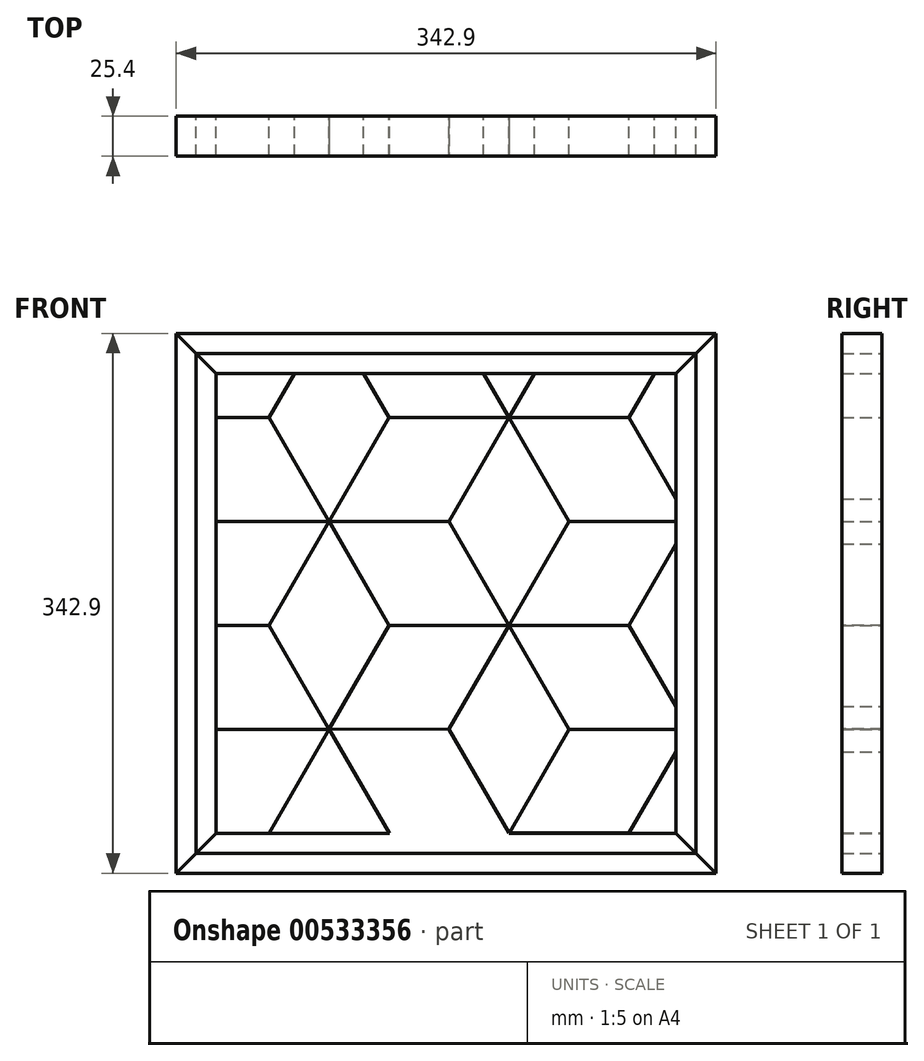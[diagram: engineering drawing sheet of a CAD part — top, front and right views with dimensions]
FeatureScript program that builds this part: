
annotation { "Feature Type Name" : "Feature", "Feature Type Description" : "" }
export const myFeature = defineFeature(function(context is Context, id is Id, definition is map)
    precondition{}
    {
        {
            var Q0;
            Q0=qCreatedBy(makeId("Front.planeOp"),FACE);
            var sketch = newSketch(context, id + "F0", { "sketchPlane" : qUnion([Q0])});
            skLineSegment(sketch, "E0.top", {"start": v(-173.38, -167.67) * mm, "end": v(169.52, -167.67) * mm});
            skLineSegment(sketch, "E0.left", {"start": v(-173.38, 175.23) * mm, "end": v(-173.38, -167.67) * mm});
            skLineSegment(sketch, "E0.right", {"start": v(169.52, 175.23) * mm, "end": v(169.52, -167.67) * mm});
            skLineSegment(sketch, "E1.0", {"start": v(-147.98, 149.83) * mm, "end": v(144.12, 149.83) * mm});
            skLineSegment(sketch, "E1.1", {"start": v(-147.98, 149.83) * mm, "end": v(-147.98, -142.27) * mm});
            skLineSegment(sketch, "E1.2", {"start": v(-147.98, -142.27) * mm, "end": v(144.12, -142.27) * mm});
            skLineSegment(sketch, "E1.3", {"start": v(144.12, 149.83) * mm, "end": v(144.12, -142.27) * mm});
            skLineSegment(sketch, "E2", {"start": v(144.12, 149.83) * mm, "end": v(169.52, 175.23) * mm});
            skLineSegment(sketch, "E3", {"start": v(169.52, -167.67) * mm, "end": v(144.12, -142.27) * mm});
            skLineSegment(sketch, "E4", {"start": v(-173.38, -167.67) * mm, "end": v(-147.98, -142.27) * mm});
            skLineSegment(sketch, "E5", {"start": v(-147.98, 149.83) * mm, "end": v(-173.38, 175.23) * mm});
            skLineSegment(sketch, "E6.0", {"start": v(-76.2, -76.14) * mm, "end": v(-38.1, -10.28) * mm});
            skLineSegment(sketch, "E6.1", {"start": v(-38.1, -10.28) * mm, "end": v(38.1, -10.28) * mm});
            skLineSegment(sketch, "E6.2", {"start": v(38.1, -10.28) * mm, "end": v(76.2, -76.27) * mm});
            skLineSegment(sketch, "E6.3", {"start": v(76.2, -76.27) * mm, "end": v(38.1, -142.27) * mm});
            skLineSegment(sketch, "E6.4", {"start": v(38.1, -142.27) * mm, "end": v(-38.02, -142.27) * mm});
            skLineSegment(sketch, "E6.5", {"start": v(-38.02, -142.27) * mm, "end": v(-76.2, -76.14) * mm});
            skLineSegment(sketch, "E7", {"start": v(-76.2, -76.14) * mm, "end": v(0, -76.27) * mm});
            skLineSegment(sketch, "E8", {"start": v(0, -76.27) * mm, "end": v(38.1, -10.28) * mm});
            skLineSegment(sketch, "E9", {"start": v(0, -76.27) * mm, "end": v(38.1, -142.27) * mm});
            skLineSegment(sketch, "E10.0", {"start": v(-114.3, -10.28) * mm, "end": v(-76.2, 55.7) * mm});
            skLineSegment(sketch, "E10.1", {"start": v(-76.2, 55.7) * mm, "end": v(0, 55.7) * mm});
            skLineSegment(sketch, "E10.2", {"start": v(0, 55.7) * mm, "end": v(38.1, -10.15) * mm});
            skLineSegment(sketch, "E10.3", {"start": v(38.1, -10.15) * mm, "end": v(0, -76.27) * mm});
            skLineSegment(sketch, "E10.4", {"start": v(0, -76.27) * mm, "end": v(-76.2, -76.14) * mm});
            skLineSegment(sketch, "E11", {"start": v(-76.2, 55.7) * mm, "end": v(-38.1, -10.28) * mm});
            skLineSegment(sketch, "E12.0", {"start": v(-38.1, -10.28) * mm, "end": v(-76.2, -76.27) * mm});
            skLineSegment(sketch, "E13", {"start": v(-114.3, -10.28) * mm, "end": v(-147.98, -10.28) * mm});
            skLineSegment(sketch, "E14", {"start": v(38.1, -10.28) * mm, "end": v(114.3, -10.28) * mm});
            skLineSegment(sketch, "E15.0", {"start": v(38.1, -10.15) * mm, "end": v(114.3, -10.15) * mm});
            skLineSegment(sketch, "E15.1", {"start": v(114.3, -10.15) * mm, "end": v(144.12, -61.8) * mm});
            skLineSegment(sketch, "E15.3", {"start": v(114.3, -142.13) * mm, "end": v(38.1, -142.13) * mm});
            skLineSegment(sketch, "E15.4", {"start": v(38.1, -142.13) * mm, "end": v(0, -76.14) * mm});
            skLineSegment(sketch, "E15.5", {"start": v(0, -76.14) * mm, "end": v(38.1, -10.15) * mm});
            skLineSegment(sketch, "E16", {"start": v(144.12, -90.48) * mm, "end": v(114.3, -142.13) * mm});
            skLineSegment(sketch, "E17", {"start": v(76.2, -76.27) * mm, "end": v(144.12, -76.27) * mm});
            skLineSegment(sketch, "E18", {"start": v(144.12, 55.85) * mm, "end": v(76.2, 55.85) * mm});
            skLineSegment(sketch, "E19", {"start": v(114.3, -10.28) * mm, "end": v(144.12, 41.5) * mm});
            skLineSegment(sketch, "E20", {"start": v(-76.2, -76.27) * mm, "end": v(-114.3, -142.27) * mm});
            skLineSegment(sketch, "E21", {"start": v(-76.2, -76.27) * mm, "end": v(-114.3, -10.28) * mm});
            skLineSegment(sketch, "E22", {"start": v(-76.2, -76.27) * mm, "end": v(-147.98, -76.27) * mm});
            skLineSegment(sketch, "E23.0", {"start": v(-38.1, -10.15) * mm, "end": v(-76.2, 55.85) * mm});
            skLineSegment(sketch, "E23.1", {"start": v(-76.2, 55.85) * mm, "end": v(-38.1, 121.84) * mm});
            skLineSegment(sketch, "E23.2", {"start": v(-38.1, 121.84) * mm, "end": v(38.1, 121.84) * mm});
            skLineSegment(sketch, "E23.3", {"start": v(38.1, 121.84) * mm, "end": v(76.2, 55.85) * mm});
            skLineSegment(sketch, "E23.4", {"start": v(76.2, 55.85) * mm, "end": v(38.1, -10.15) * mm});
            skLineSegment(sketch, "E23.5", {"start": v(38.1, -10.15) * mm, "end": v(-38.1, -10.15) * mm});
            skLineSegment(sketch, "E24.0", {"start": v(0, 55.85) * mm, "end": v(-76.2, 55.85) * mm});
            skLineSegment(sketch, "E24.1", {"start": v(-76.2, 55.85) * mm, "end": v(-114.3, 121.84) * mm});
            skLineSegment(sketch, "E24.2", {"start": v(-114.3, 121.84) * mm, "end": v(-98.14, 149.83) * mm});
            skLineSegment(sketch, "E24.4", {"start": v(21.94, 149.83) * mm, "end": v(38.1, 121.84) * mm});
            skLineSegment(sketch, "E24.5", {"start": v(38.1, 121.84) * mm, "end": v(0, 55.85) * mm});
            skLineSegment(sketch, "E25.1", {"start": v(76.2, 55.85) * mm, "end": v(38.1, 121.84) * mm});
            skLineSegment(sketch, "E25.2", {"start": v(38.1, 121.84) * mm, "end": v(54.26, 149.83) * mm});
            skLineSegment(sketch, "E26.0", {"start": v(-76.2, 55.85) * mm, "end": v(-147.98, 55.85) * mm});
            skLineSegment(sketch, "E26.4", {"start": v(-54.26, 149.83) * mm, "end": v(-38.1, 121.84) * mm});
            skLineSegment(sketch, "E26.5", {"start": v(-38.1, 121.84) * mm, "end": v(-76.2, 55.85) * mm});
            skLineSegment(sketch, "E27.trimOffspring", {"start": v(-173.38, 175.23) * mm, "end": v(169.52, 175.23) * mm});
            skLineSegment(sketch, "E28", {"start": v(-114.3, 121.84) * mm, "end": v(-147.98, 121.84) * mm});
            skLineSegment(sketch, "E29", {"start": v(38.1, 121.84) * mm, "end": v(114.3, 121.84) * mm});
            skLineSegment(sketch, "E30", {"start": v(114.3, 121.84) * mm, "end": v(144.12, 70.2) * mm});
            skLineSegment(sketch, "E31", {"start": v(114.3, 121.84) * mm, "end": v(130.46, 149.83) * mm});
            skLineSegment(sketch, "E32", {"start": v(-160.68, 162.53) * mm, "end": v(156.82, 162.53) * mm});
            skLineSegment(sketch, "E33", {"start": v(156.82, 162.53) * mm, "end": v(156.82, -154.97) * mm});
            skLineSegment(sketch, "E34", {"start": v(156.82, -154.97) * mm, "end": v(-160.68, -154.97) * mm});
            skLineSegment(sketch, "E35", {"start": v(-160.68, -154.97) * mm, "end": v(-160.68, 162.53) * mm});
            skSolve(sketch);
        }
        {
            var Q0;
            {var subQ0=sQuery(id+"F0.wireOp",EDGE,"E0.left");Q0=makeQuery(id+"F0.imprint","IMPRINT",FACE,{"disambiguationData":[TD([[makeQuery(id+"F0.imprint","IMPRINT",EDGE,{"derivedFrom":subQ0}),1.0]])]});}
            var Q1;
            {var subQ0=sQuery(id+"F0.wireOp",EDGE,"E0.right");Q1=makeQuery(id+"F0.imprint","IMPRINT",FACE,{"disambiguationData":[TD([[makeQuery(id+"F0.imprint","IMPRINT",EDGE,{"derivedFrom":subQ0}),-1.0]])]});}
            var Q2;
            {var subQ4=sQuery(id+"F0.wireOp",EDGE,"E6.4");Q2=makeQuery(id+"F0.imprint","IMPRINT",FACE,{"disambiguationData":[TD([[makeQuery(id+"F0.imprint","IMPRINT",EDGE,{"derivedFrom":subQ4}),1.0]])]});}
            var Q3;
            {var subQ10=sQuery(id+"F0.wireOp",EDGE,"E32");Q3=makeQuery(id+"F0.imprint","IMPRINT",FACE,{"disambiguationData":[TD([[makeQuery(id+"F0.imprint","IMPRINT",EDGE,{"derivedFrom":subQ10}),-1.0]])]});}
            extrude(context, id + "F1", {"entities" : qUnion([Q0, Q1, Q2, Q3]), "depth" : 25.4 * mm, "offsetDistance" : 25.4 * mm});
        }
        {
            var Q0;
            {var subQ0=sQuery(id+"F0.wireOp",EDGE,"E27.trimOffspring");Q0=makeQuery(id+"F0.imprint","IMPRINT",FACE,{"disambiguationData":[TD([[makeQuery(id+"F0.imprint","IMPRINT",EDGE,{"derivedFrom":subQ0}),-1.0]])]});}
            var Q1;
            {var subQ9=sQuery(id+"F0.wireOp",EDGE,"E35");Q1=makeQuery(id+"F0.imprint","IMPRINT",FACE,{"disambiguationData":[TD([[makeQuery(id+"F0.imprint","IMPRINT",EDGE,{"derivedFrom":subQ9}),-1.0]])]});}
            var Q2;
            {var subQ11=sQuery(id+"F0.wireOp",EDGE,"E33");Q2=makeQuery(id+"F0.imprint","IMPRINT",FACE,{"disambiguationData":[TD([[makeQuery(id+"F0.imprint","IMPRINT",EDGE,{"derivedFrom":subQ11}),-1.0]])]});}
            var Q3;
            {var subQ0=sQuery(id+"F0.wireOp",EDGE,"E0.top");Q3=makeQuery(id+"F0.imprint","IMPRINT",FACE,{"disambiguationData":[TD([[makeQuery(id+"F0.imprint","IMPRINT",EDGE,{"derivedFrom":subQ0}),1.0]])]});}
            var Q4;
            Q4=makeQuery(id+"F0.imprint","IMPRINT",FACE,{"disambiguationData":[TD([[makeQuery(id+"F0.imprint","IMPRINT",EDGE,{"derivedFrom":sQuery(id+"F0.wireOp",EDGE,"E24.1")}),-1.0]])]});
            var Q5;
            {var subQ0=sQuery(id+"F0.wireOp",EDGE,"E24.4");Q5=makeQuery(id+"F0.imprint","IMPRINT",FACE,{"disambiguationData":[TD([[makeQuery(id+"F0.imprint","IMPRINT",EDGE,{"derivedFrom":subQ0}),1.0]])]});}
            var Q6;
            {var subQ0=sQuery(id+"F0.wireOp",EDGE,"E10.2");Q6=makeQuery(id+"F0.imprint","IMPRINT",FACE,{"disambiguationData":[TD([[makeQuery(id+"F0.imprint","IMPRINT",EDGE,{"derivedFrom":subQ0}),1.0]])]});}
            var Q7;
            {var subQ1=sQuery(id+"F0.wireOp",EDGE,"E6.0");Q7=makeQuery(id+"F0.imprint","IMPRINT",FACE,{"disambiguationData":[TD([[makeQuery(id+"F0.imprint","IMPRINT",EDGE,{"derivedFrom":subQ1}),1.0]])]});}
            var Q8;
            {var subQ6=sQuery(id+"F0.wireOp",EDGE,"E6.2");Q8=makeQuery(id+"F0.imprint","IMPRINT",FACE,{"disambiguationData":[TD([[makeQuery(id+"F0.imprint","IMPRINT",EDGE,{"derivedFrom":subQ6}),-1.0]])]});}
            var Q9;
            {var subQ3=sQuery(id+"F0.wireOp",EDGE,"E20");Q9=makeQuery(id+"F0.imprint","IMPRINT",FACE,{"disambiguationData":[TD([[makeQuery(id+"F0.imprint","IMPRINT",EDGE,{"derivedFrom":subQ3}),1.0]])]});}
            extrude(context, id + "F2", {"entities" : qUnion([Q0, Q1, Q2, Q3, Q4, Q5, Q6, Q7, Q8, Q9]), "depth" : 25.4 * mm, "offsetDistance" : 25.4 * mm});
        }
        {
            var Q0;
            Q0=makeQuery(id+"F2.opExtrude","CAP_FACE",FACE,{"disambiguationData":[OSD([sQuery(id+"F0.wireOp",EDGE,"E1.0"),sQuery(id+"F0.wireOp",EDGE,"E24.4"),sQuery(id+"F0.wireOp",EDGE,"E25.2")])],"isStart":false});
            var Q1;
            {var subQ0=sQuery(id+"F0.wireOp",EDGE,"E10.2");Q1=makeQuery(id+"F0.imprint","IMPRINT",FACE,{"disambiguationData":[TD([[makeQuery(id+"F0.imprint","IMPRINT",EDGE,{"derivedFrom":subQ0}),-1.0]])]});}
            var Q2;
            {var subQ1=sQuery(id+"F0.wireOp",EDGE,"E10.0");Q2=makeQuery(id+"F0.imprint","IMPRINT",FACE,{"disambiguationData":[TD([[makeQuery(id+"F0.imprint","IMPRINT",EDGE,{"derivedFrom":subQ1}),1.0]])]});}
            var Q3;
            {var subQ3=sQuery(id+"F0.wireOp",EDGE,"E24.2");Q3=makeQuery(id+"F0.imprint","IMPRINT",FACE,{"disambiguationData":[TD([[makeQuery(id+"F0.imprint","IMPRINT",EDGE,{"derivedFrom":subQ3}),1.0]])]});}
            var Q4;
            {var subQ4=sQuery(id+"F0.wireOp",EDGE,"E30");Q4=makeQuery(id+"F0.imprint","IMPRINT",FACE,{"disambiguationData":[TD([[makeQuery(id+"F0.imprint","IMPRINT",EDGE,{"derivedFrom":subQ4}),1.0]])]});}
            var Q5;
            {var subQ0=sQuery(id+"F0.wireOp",EDGE,"E16");Q5=makeQuery(id+"F0.imprint","IMPRINT",FACE,{"disambiguationData":[TD([[makeQuery(id+"F0.imprint","IMPRINT",EDGE,{"derivedFrom":subQ0}),-1.0]])]});}
            var Q6;
            {var subQ5=sQuery(id+"F0.wireOp",EDGE,"E6.4");Q6=makeQuery(id+"F0.imprint","IMPRINT",FACE,{"disambiguationData":[TD([[makeQuery(id+"F0.imprint","IMPRINT",EDGE,{"derivedFrom":subQ5}),-1.0]])]});}
            var Q7;
            {var subQ4=sQuery(id+"F0.wireOp",EDGE,"E20");Q7=makeQuery(id+"F0.imprint","IMPRINT",FACE,{"disambiguationData":[TD([[makeQuery(id+"F0.imprint","IMPRINT",EDGE,{"derivedFrom":subQ4}),-1.0]])]});}
            var Q8;
            {var subQ1=sQuery(id+"F0.wireOp",EDGE,"E15.0");Q8=makeQuery(id+"F0.imprint","IMPRINT",FACE,{"disambiguationData":[TD([[makeQuery(id+"F0.imprint","IMPRINT",EDGE,{"derivedFrom":subQ1}),1.0]])]});}
            extrude(context, id + "F3", {"entities" : qUnion([Q0, Q1, Q2, Q3, Q4, Q5, Q6, Q7, Q8]), "depth" : 25.4 * mm, "offsetDistance" : 25.4 * mm});
        }
        {
            var Q0;
            {var subQ0=sQuery(id+"F0.wireOp",EDGE,"E13");Q0=makeQuery(id+"F0.imprint","IMPRINT",FACE,{"disambiguationData":[TD([[makeQuery(id+"F0.imprint","IMPRINT",EDGE,{"derivedFrom":subQ0}),1.0]])]});}
            var Q1;
            {var subQ0=sQuery(id+"F0.wireOp",EDGE,"E12.0");var subQ1=makeQuery(id+"F0.imprint","INTERSECT",VERTEX,{"derivedFrom":[sQuery(id+"F0.wireOp",EDGE,"E6.0"),subQ0]});Q1=makeQuery(id+"F0.imprint","IMPRINT",FACE,{"disambiguationData":[TD([[makeQuery(id+"F0.imprint","IMPRINT",EDGE,{"disambiguationData":[TD([[subQ1,-1.0]])],"derivedFrom":subQ0}),1.0]])]});}
            var Q2;
            Q2=makeQuery(id+"F0.imprint","IMPRINT",FACE,{"disambiguationData":[TD([[makeQuery(id+"F0.imprint","IMPRINT",EDGE,{"derivedFrom":sQuery(id+"F0.wireOp",EDGE,"E6.2")}),1.0]])]});
            var Q3;
            {var subQ0=sQuery(id+"F0.wireOp",EDGE,"E16");Q3=makeQuery(id+"F0.imprint","IMPRINT",FACE,{"disambiguationData":[TD([[makeQuery(id+"F0.imprint","IMPRINT",EDGE,{"derivedFrom":subQ0}),1.0]])]});}
            var Q4;
            Q4=makeQuery(id+"F3.opExtrude","CAP_FACE",FACE,{"disambiguationData":[OSD([sQuery(id+"F0.wireOp",EDGE,"E1.0"),sQuery(id+"F0.wireOp",EDGE,"E1.3"),sQuery(id+"F0.wireOp",EDGE,"E30"),sQuery(id+"F0.wireOp",EDGE,"E31")])],"isStart":false});
            var Q5;
            Q5=makeQuery(id+"F0.imprint","IMPRINT",FACE,{"disambiguationData":[TD([[makeQuery(id+"F0.imprint","IMPRINT",EDGE,{"derivedFrom":sQuery(id+"F0.wireOp",EDGE,"E23.2")}),1.0]])]});
            var Q6;
            Q6=makeQuery(id+"F0.imprint","IMPRINT",FACE,{"disambiguationData":[TD([[makeQuery(id+"F0.imprint","IMPRINT",EDGE,{"derivedFrom":sQuery(id+"F0.wireOp",EDGE,"E24.1")}),1.0]])]});
            extrude(context, id + "F4", {"entities" : qUnion([Q0, Q1, Q2, Q3, Q4, Q5, Q6]), "depth" : 25.4 * mm, "offsetDistance" : 25.4 * mm});
        }
        {
            var Q0;
            Q0=makeQuery(id+"F0.imprint","IMPRINT",FACE,{"disambiguationData":[TD([[makeQuery(id+"F0.imprint","IMPRINT",EDGE,{"derivedFrom":sQuery(id+"F0.wireOp",EDGE,"E23.2")}),-1.0]])]});
            var Q1;
            {var subQ0=sQuery(id+"F0.wireOp",EDGE,"E18");Q1=makeQuery(id+"F0.imprint","IMPRINT",FACE,{"disambiguationData":[TD([[makeQuery(id+"F0.imprint","IMPRINT",EDGE,{"derivedFrom":subQ0}),-1.0]])]});}
            extrude(context, id + "F5", {"entities" : qUnion([Q0, Q1]), "depth" : 25.4 * mm, "offsetDistance" : 25.4 * mm});
        }
        {
            var Q0;
            {var subQ0=sQuery(id+"F0.wireOp",EDGE,"E25.2");Q0=makeQuery(id+"F0.imprint","IMPRINT",FACE,{"disambiguationData":[TD([[makeQuery(id+"F0.imprint","IMPRINT",EDGE,{"derivedFrom":subQ0}),-1.0]])]});}
            extrude(context, id + "F6", {"entities" : qUnion([Q0]), "depth" : 25.4 * mm, "offsetDistance" : 25.4 * mm});
        }
        {
            var Q0;
            Q0=makeQuery(id+"F6.opExtrude","CAP_FACE",FACE,{"disambiguationData":[OSD([sQuery(id+"F0.wireOp",EDGE,"E1.0"),sQuery(id+"F0.wireOp",EDGE,"E25.2"),sQuery(id+"F0.wireOp",EDGE,"E29"),sQuery(id+"F0.wireOp",EDGE,"E31")])],"isStart":false});
            extrude(context, id + "F7", {"entities" : qUnion([Q0]), "depth" : 25.4 * mm, "offsetDistance" : 25.4 * mm});
        }
        {
            var Q0;
            Q0=makeQuery(id+"F7.opExtrude","SWEPT_BODY",BODY,{"disambiguationData":[OSD([sQuery(id+"F0.wireOp",EDGE,"E1.0"),sQuery(id+"F0.wireOp",EDGE,"E25.2"),sQuery(id+"F0.wireOp",EDGE,"E29"),sQuery(id+"F0.wireOp",EDGE,"E31")])]});
            var Q1;
            Q1=makeQuery(id+"F4.opExtrude","SWEPT_BODY",BODY,{"disambiguationData":[OSD([sQuery(id+"F0.wireOp",EDGE,"E1.0"),sQuery(id+"F0.wireOp",EDGE,"E1.3"),sQuery(id+"F0.wireOp",EDGE,"E30"),sQuery(id+"F0.wireOp",EDGE,"E31")])]});
            var Q2;
            Q2=makeQuery(id+"F3.opExtrude","SWEPT_BODY",BODY,{"disambiguationData":[OSD([sQuery(id+"F0.wireOp",EDGE,"E1.0"),sQuery(id+"F0.wireOp",EDGE,"E24.4"),sQuery(id+"F0.wireOp",EDGE,"E25.2")])]});
            deleteBodies(context, id + "F8", {"entities" : qUnion([Q0, Q1, Q2])});
        }
        {
            var Q0;
            {var subQ0=sQuery(id+"F0.wireOp",EDGE,"E15.1");var subQ1=sQuery(id+"F0.wireOp",EDGE,"E1.3");var subQ2=makeQuery(id+"F0.imprint","INTERSECT",VERTEX,{"derivedFrom":[subQ1,subQ0]});Q0=makeQuery(id+"F0.imprint","IMPRINT",FACE,{"disambiguationData":[TD([[makeQuery(id+"F0.imprint","IMPRINT",EDGE,{"disambiguationData":[TD([[subQ2,1.0]])],"derivedFrom":subQ1}),-1.0]])]});}
            extrude(context, id + "F9", {"entities" : qUnion([Q0]), "depth" : 25.4 * mm, "offsetDistance" : 25.4 * mm});
        }
    });
